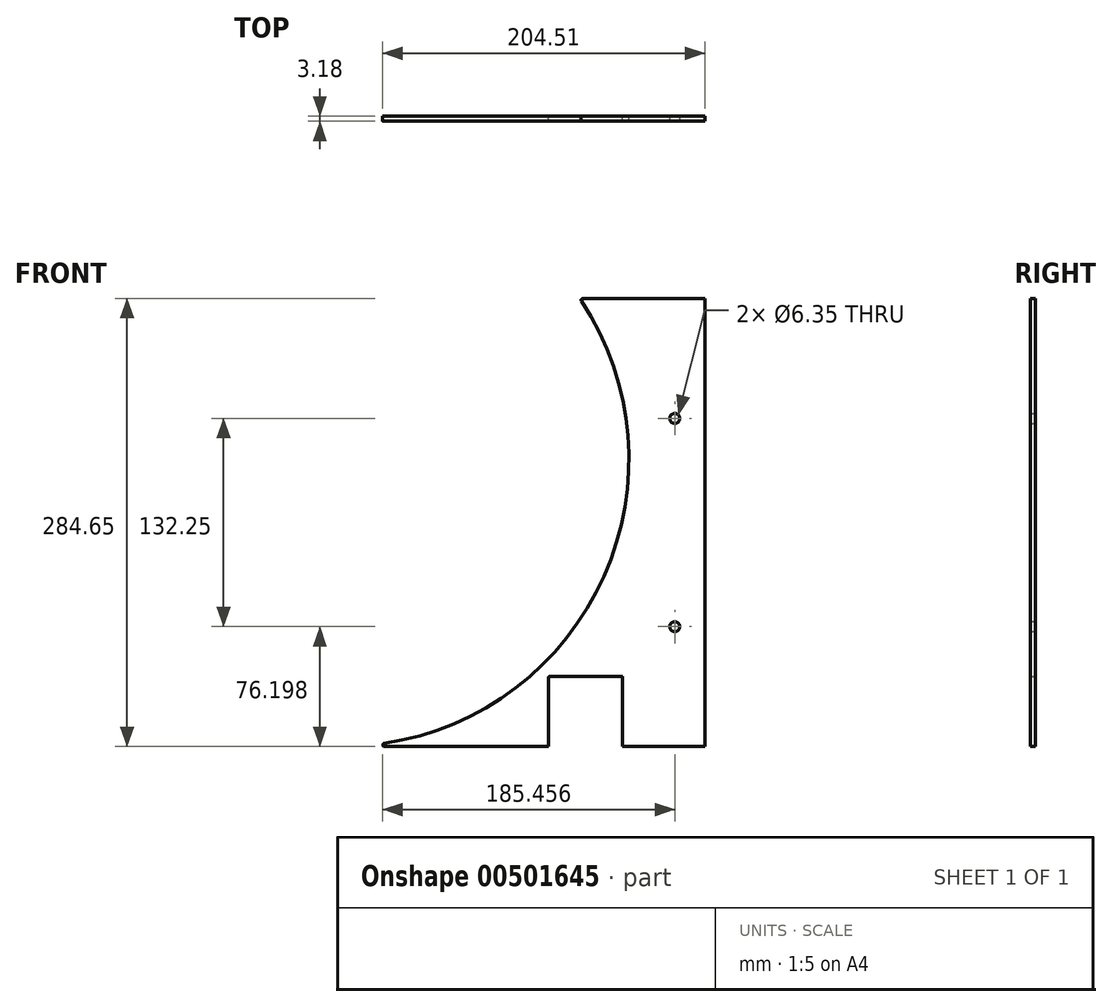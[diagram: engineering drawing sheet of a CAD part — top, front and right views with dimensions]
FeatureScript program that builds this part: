
annotation { "Feature Type Name" : "Feature", "Feature Type Description" : "" }
export const myFeature = defineFeature(function(context is Context, id is Id, definition is map)
    precondition{}
    {
        {
            var Q0;
            Q0=qCreatedBy(makeId("Front.planeOp"),FACE);
            var sketch = newSketch(context, id + "F0", { "sketchPlane" : qUnion([Q0])});
            skArc(sketch, "E0", {"start": v(0, -182.56) * mm, "mid": v(161.2, -85.7) * mm, "end": v(151.35, 102.09) * mm});
            skCircle(sketch, "E1", {"center": v(0, 0) * mm, "radius": 61.91 * mm, "construction": true});
            skLineSegment(sketch, "E2", {"start": v(0, 0) * mm, "end": v(0, -298.83) * mm, "construction": true});
            skLineSegment(sketch, "E3", {"start": v(0, -182.56) * mm, "end": v(131.59, -182.56) * mm});
            skLineSegment(sketch, "E4", {"start": v(230.73, -182.56) * mm, "end": v(230.73, 102.09) * mm});
            skLineSegment(sketch, "E5", {"start": v(230.73, 102.09) * mm, "end": v(151.35, 102.09) * mm});
            skLineSegment(sketch, "E6", {"start": v(0, 0) * mm, "end": v(377.6, 0) * mm, "construction": true});
            skLineSegment(sketch, "E7", {"start": v(182.56, 0) * mm, "end": v(151.35, 102.09) * mm, "construction": true});
            skLineSegment(sketch, "E8", {"start": v(182.56, 0) * mm, "end": v(182.56, 254) * mm, "construction": true});
            skCircle(sketch, "E9", {"center": v(173.38, 82.7) * mm, "radius": 3.18 * mm, "construction": true});
            skCircle(sketch, "E10.1.0", {"center": v(191.56, 14.24) * mm, "radius": 3.18 * mm, "construction": true});
            skCircle(sketch, "E10.2.0", {"center": v(183.7, -56.16) * mm, "radius": 3.18 * mm, "construction": true});
            skCircle(sketch, "E10.3.0", {"center": v(150.85, -118.92) * mm, "radius": 3.18 * mm, "construction": true});
            skCircle(sketch, "E10.4.0", {"center": v(97.5, -165.5) * mm, "radius": 3.18 * mm, "construction": true});
            skLineSegment(sketch, "E10.anchor1", {"start": v(0, 0) * mm, "end": v(173.38, 82.7) * mm, "construction": true});
            skLineSegment(sketch, "E10.anchor2", {"start": v(0, 0) * mm, "end": v(97.5, -165.5) * mm, "construction": true});
            skLineSegment(sketch, "E11.bottom", {"start": v(132.22, -137.96) * mm, "end": v(177.94, -137.96) * mm});
            skLineSegment(sketch, "E11.left", {"start": v(131.59, -138.6) * mm, "end": v(131.59, -182.56) * mm});
            skLineSegment(sketch, "E11.right", {"start": v(178.58, -138.6) * mm, "end": v(178.58, -182.56) * mm});
            skLineSegment(sketch, "E12", {"start": v(155.08, -137.96) * mm, "end": v(155.08, -182.56) * mm, "construction": true});
            skPoint(sketch, "E13", {"position": v(155.08, -160.26) * mm});
            skLineSegment(sketch, "E14.trimOffspring", {"start": v(178.58, -182.56) * mm, "end": v(230.73, -182.56) * mm});
            skPoint(sketch, "E15.visualSharp", {"position": v(131.59, -137.96) * mm});
            skArc(sketch, "E15.filletArc", {"start": v(132.22, -137.96) * mm, "mid": v(131.77, -138.15) * mm, "end": v(131.59, -138.6) * mm});
            skPoint(sketch, "E16.visualSharp", {"position": v(178.58, -137.96) * mm});
            skArc(sketch, "E16.filletArc", {"start": v(178.58, -138.6) * mm, "mid": v(178.4, -138.15) * mm, "end": v(177.94, -137.96) * mm});
            skLineSegment(sketch, "E17", {"start": v(211.68, 102.09) * mm, "end": v(211.68, -182.56) * mm, "construction": true});
            skLineSegment(sketch, "E18", {"start": v(230.73, 25.89) * mm, "end": v(180.72, 25.89) * mm, "construction": true});
            skLineSegment(sketch, "E19", {"start": v(148.38, -106.36) * mm, "end": v(230.73, -106.36) * mm, "construction": true});
            skCircle(sketch, "E20", {"center": v(211.68, -106.36) * mm, "radius": 3.18 * mm});
            skCircle(sketch, "E21", {"center": v(211.68, 25.89) * mm, "radius": 3.18 * mm});
            skLineSegment(sketch, "E22", {"start": v(0, 0) * mm, "end": v(151.35, 102.09) * mm, "construction": true});
            skSolve(sketch);
        }
        {
            var Q0;
            Q0=qSketchRegion(id+"F0",true);
            extrude(context, id + "F1", {"entities" : qUnion([Q0]), "depth" : 3.17 * mm});
        }
        {
            var Q0;
            Q0=makeQuery(id+"F1.opExtrude","CAP_FACE",FACE,{"disambiguationData":[OSD([sQuery(id+"F0.wireOp",EDGE,"E0"),sQuery(id+"F0.wireOp",EDGE,"E3"),sQuery(id+"F0.wireOp",EDGE,"E4"),sQuery(id+"F0.wireOp",EDGE,"E5"),sQuery(id+"F0.wireOp",EDGE,"E11.bottom"),sQuery(id+"F0.wireOp",EDGE,"E11.left"),sQuery(id+"F0.wireOp",EDGE,"E11.right"),sQuery(id+"F0.wireOp",EDGE,"E14.trimOffspring"),sQuery(id+"F0.wireOp",EDGE,"E15.filletArc"),sQuery(id+"F0.wireOp",EDGE,"E16.filletArc")])],"isStart":false});
            var sketch = newSketch(context, id + "F2", { "sketchPlane" : qUnion([Q0])});
            skLineSegment(sketch, "E23", {"start": v(86.22, -160.92) * mm, "end": v(87, -162.32) * mm});
            skLineSegment(sketch, "E24", {"start": v(87, -162.32) * mm, "end": v(84.93, -163.45) * mm});
            skLineSegment(sketch, "E25", {"start": v(84.93, -163.45) * mm, "end": v(86.58, -166.46) * mm});
            skLineSegment(sketch, "E26", {"start": v(86.58, -166.46) * mm, "end": v(88.64, -165.33) * mm});
            skLineSegment(sketch, "E27", {"start": v(88.64, -165.33) * mm, "end": v(89.52, -166.93) * mm});
            skLineSegment(sketch, "E28", {"start": v(89.52, -166.93) * mm, "end": v(92.64, -165.22) * mm});
            skLineSegment(sketch, "E29", {"start": v(92.64, -165.22) * mm, "end": v(91.76, -163.62) * mm});
            skLineSegment(sketch, "E30", {"start": v(91.76, -163.62) * mm, "end": v(93.82, -162.49) * mm});
            skLineSegment(sketch, "E31", {"start": v(93.82, -162.49) * mm, "end": v(92.17, -159.48) * mm});
            skLineSegment(sketch, "E32", {"start": v(92.17, -159.48) * mm, "end": v(90.11, -160.61) * mm});
            skLineSegment(sketch, "E33", {"start": v(90.11, -160.61) * mm, "end": v(89.34, -159.2) * mm});
            skLineSegment(sketch, "E34", {"start": v(164.06, 80.1) * mm, "end": v(165.5, 80.78) * mm});
            skLineSegment(sketch, "E35", {"start": v(165.5, 80.78) * mm, "end": v(164.49, 82.9) * mm});
            skLineSegment(sketch, "E36", {"start": v(164.49, 82.9) * mm, "end": v(167.59, 84.38) * mm});
            skLineSegment(sketch, "E37", {"start": v(167.59, 84.38) * mm, "end": v(168.6, 82.26) * mm});
            skLineSegment(sketch, "E38", {"start": v(168.6, 82.26) * mm, "end": v(170.25, 83.04) * mm});
            skLineSegment(sketch, "E39", {"start": v(170.25, 83.04) * mm, "end": v(171.78, 79.83) * mm});
            skLineSegment(sketch, "E40", {"start": v(171.78, 79.83) * mm, "end": v(170.12, 79.04) * mm});
            skLineSegment(sketch, "E41", {"start": v(170.12, 79.04) * mm, "end": v(171.14, 76.92) * mm});
            skLineSegment(sketch, "E42", {"start": v(171.14, 76.92) * mm, "end": v(168.04, 75.45) * mm});
            skLineSegment(sketch, "E43", {"start": v(168.04, 75.45) * mm, "end": v(167.03, 77.57) * mm});
            skLineSegment(sketch, "E44", {"start": v(167.03, 77.57) * mm, "end": v(165.58, 76.88) * mm});
            skSolve(sketch);
        }
        {
            var Q0;
            Q0=makeQuery(id+"F1.opExtrude","SWEPT_EDGE",EDGE,{"disambiguationData":[OSD([sQuery(id+"F0.wireOp",EDGE,"E0"),sQuery(id+"F0.wireOp",EDGE,"E5")])]});
            var Q1;
            Q1=makeQuery(id+"F1.opExtrude","SWEPT_EDGE",EDGE,{"disambiguationData":[OSD([sQuery(id+"F0.wireOp",EDGE,"E0"),sQuery(id+"F0.wireOp",EDGE,"E3")])]});
            fillet(context, id + "F3", {"entities" : qUnion([Q0, Q1]), "radius" : 1.02 * mm, "tangentPropagation" : true, "allowEdgeOverflow" : false});
        }
    });
